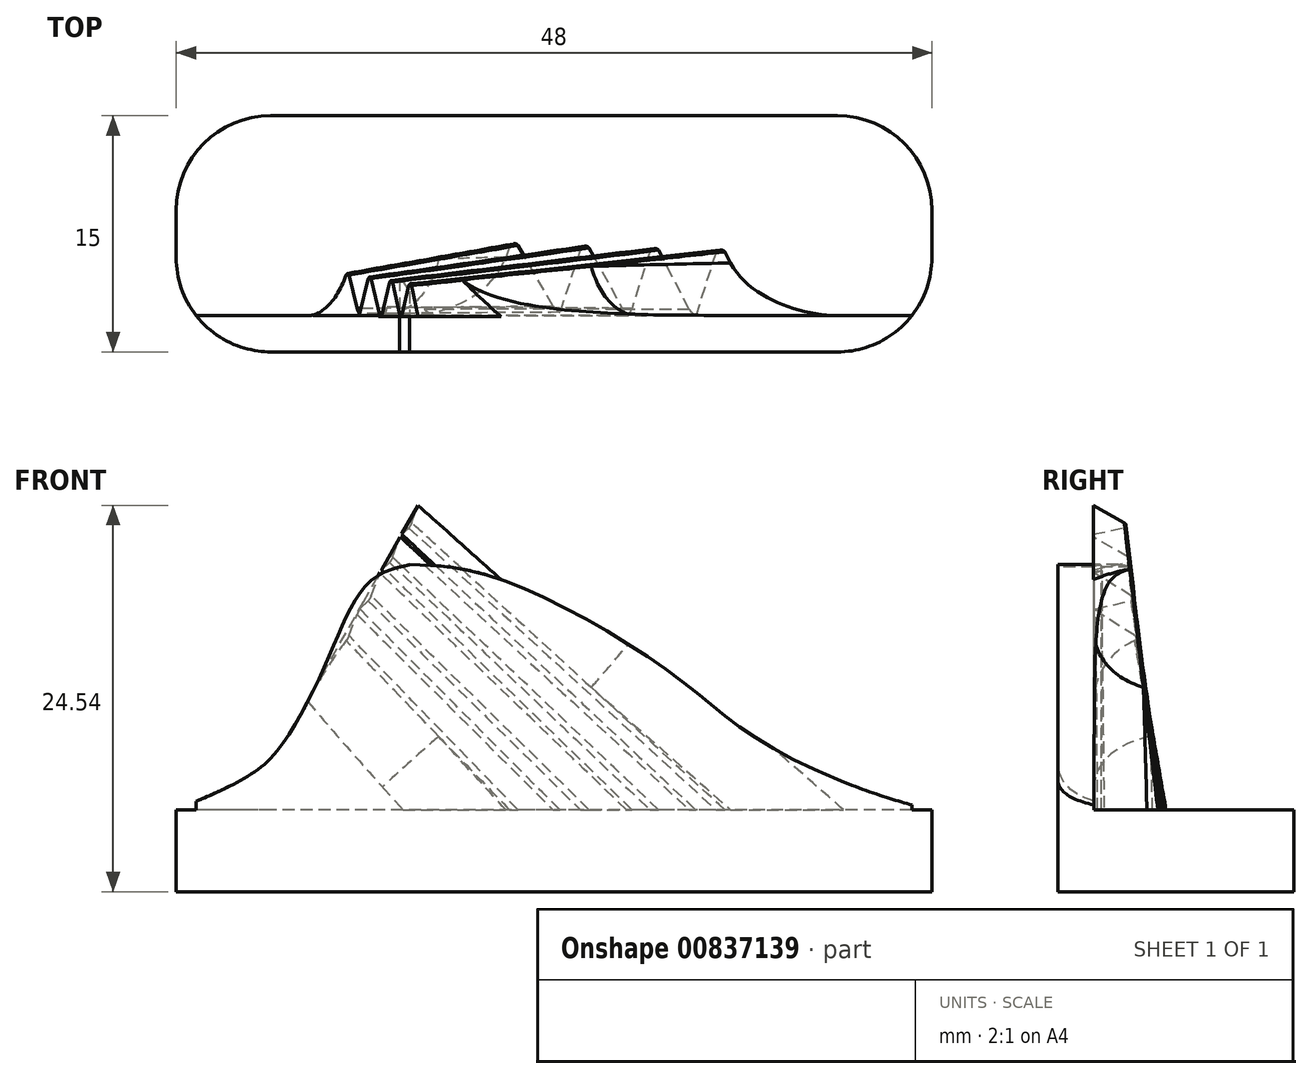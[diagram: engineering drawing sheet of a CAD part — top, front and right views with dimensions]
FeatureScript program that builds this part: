
annotation { "Feature Type Name" : "Feature", "Feature Type Description" : "" }
export const myFeature = defineFeature(function(context is Context, id is Id, definition is map)
    precondition{}
    {
        {
            var Q0;
            Q0=qCreatedBy(makeId("Top.planeOp"),FACE);
            var sketch = newSketch(context, id + "F0", { "sketchPlane" : qUnion([Q0])});
            skLineSegment(sketch, "E0.bottom", {"start": v(18, 7.5) * mm, "end": v(-18, 7.5) * mm});
            skLineSegment(sketch, "E0.top", {"start": v(18, -7.5) * mm, "end": v(-18, -7.5) * mm});
            skLineSegment(sketch, "E0.left", {"start": v(24, 1.5) * mm, "end": v(24, -1.5) * mm});
            skLineSegment(sketch, "E0.right", {"start": v(-24, 1.5) * mm, "end": v(-24, -1.5) * mm});
            skPoint(sketch, "E0.middle", {"position": v(0, 0) * mm});
            skPoint(sketch, "E1.visualSharp", {"position": v(-24, 7.5) * mm});
            skArc(sketch, "E1.filletArc", {"start": v(-18, 7.5) * mm, "mid": v(-22.24, 5.74) * mm, "end": v(-24, 1.5) * mm});
            skPoint(sketch, "E2.visualSharp", {"position": v(-24, -7.5) * mm});
            skArc(sketch, "E2.filletArc", {"start": v(-24, -1.5) * mm, "mid": v(-22.24, -5.74) * mm, "end": v(-18, -7.5) * mm});
            skPoint(sketch, "E3.visualSharp", {"position": v(24, 7.5) * mm});
            skArc(sketch, "E3.filletArc", {"start": v(24, 1.5) * mm, "mid": v(22.24, 5.74) * mm, "end": v(18, 7.5) * mm});
            skPoint(sketch, "E4.visualSharp", {"position": v(24, -7.5) * mm});
            skArc(sketch, "E4.filletArc", {"start": v(18, -7.5) * mm, "mid": v(22.24, -5.74) * mm, "end": v(24, -1.5) * mm});
            skPoint(sketch, "E5", {"position": v(-18, 0) * mm});
            skPoint(sketch, "E6", {"position": v(18, 0) * mm});
            skSolve(sketch);
        }
        {
            var Q0;
            Q0=qCreatedBy(makeId("Right.planeOp"),FACE);
            var sketch = newSketch(context, id + "F1", { "sketchPlane" : qUnion([Q0])});
            skLineSegment(sketch, "E7", {"start": v(-7.5, 0) * mm, "end": v(-7.5, 5.2) * mm});
            skLineSegment(sketch, "E8", {"start": v(-7.5, 5.2) * mm, "end": v(7.5, 5.2) * mm});
            skLineSegment(sketch, "E9", {"start": v(7.5, 5.2) * mm, "end": v(7.5, 0) * mm});
            skLineSegment(sketch, "E10", {"start": v(-7.5, 0) * mm, "end": v(-5.5, 0) * mm});
            skLineSegment(sketch, "E11", {"start": v(7.5, 0) * mm, "end": v(5.5, 0) * mm});
            skLineSegment(sketch, "E12", {"start": v(5.5, 0) * mm, "end": v(-5.5, 0) * mm});
            skSolve(sketch);
        }
        {
            var Q0;
            Q0=makeQuery(id+"F1.imprint","IMPRINT",FACE,{"disambiguationData":[TD([[makeQuery(id+"F1.imprint","IMPRINT",EDGE,{"derivedFrom":sQuery(id+"F1.wireOp",EDGE,"E7")}),-1.0]])]});
            extrude(context, id + "F2", {"entities" : qUnion([Q0]), "endBound" : BoundingType.SYMMETRIC, "depth" : 48 * mm, "offsetDistance" : 25 * mm});
        }
        {
            var Q0;
            Q0=makeQuery(id+"F2.opExtrude","SWEPT_FACE",FACE,{"disambiguationData":[OSD([sQuery(id+"F1.wireOp",EDGE,"E7")])]});
            var sketch = newSketch(context, id + "F3", { "sketchPlane" : qUnion([Q0])});
            skFitSpline(sketch, "E13", {"points": [v(-9.17, 20.78) * mm, v(-1.79, 19.2) * mm, v(7.48, 13.86) * mm, v(13.06, 9.62) * mm, v(24, 5.2) * mm], "startDerivative": vector(37.37, 0) * mm, "endDerivative": vector(42.07, -9.63) * mm});
            skFitSpline(sketch, "E14", {"points": [v(-9.17, 20.78) * mm, v(-11.22, 20.07) * mm, v(-12.79, 18.26) * mm, v(-14.28, 14.96) * mm, v(-16.72, 10.17) * mm, v(-19.07, 7.58) * mm, v(-24, 5.2) * mm], "startDerivative": vector(-16.72, -3.76) * mm, "endDerivative": vector(-25.62, -11.21) * mm});
            skLineSegment(sketch, "E15", {"start": v(-24, 5.2) * mm, "end": v(24, 5.2) * mm});
            skSolve(sketch);
        }
        {
            var Q0;
            {var subQ6=sQuery(id+"F3.wireOp",EDGE,"E13");Q0=makeQuery(id+"F3.imprint","IMPRINT",FACE,{"disambiguationData":[TD([[makeQuery(id+"F3.imprint","IMPRINT",EDGE,{"derivedFrom":subQ6}),-1.0]])]});}
            extrude(context, id + "F4", {"entities" : qUnion([Q0]), "operationType" : NewBodyOperationType.ADD, "oppositeDirection" : true, "depth" : 2.3 * mm, "offsetDistance" : 25 * mm});
        }
        {
            var Q0;
            Q0=makeQuery(id+"F2.opExtrude","CAP_EDGE",EDGE,{"disambiguationData":[OSD([sQuery(id+"F1.wireOp",EDGE,"E7")])],"isStart":true});
            var Q1;
            Q1=makeQuery(id+"F2.opExtrude","CAP_EDGE",EDGE,{"disambiguationData":[OSD([sQuery(id+"F1.wireOp",EDGE,"E7")])],"isStart":false});
            fillet(context, id + "F5", {"entities" : qUnion([Q0, Q1]), "radius" : 6 * mm, "tangentPropagation" : true, "allowEdgeOverflow" : false});
        }
        {
            var Q0;
            Q0=makeQuery(id+"F4.opExtrude","CAP_EDGE",EDGE,{"disambiguationData":[OSD([sQuery(id+"F3.wireOp",EDGE,"E14")])],"isStart":true});
            cPoint(context, id + "F6", {"entities" : qUnion([Q0]), "parameter" : 0.5});
        }
        {
            var Q0;
            Q0=makeQuery(id+"F4.opExtrude","CAP_EDGE",EDGE,{"disambiguationData":[OSD([sQuery(id+"F3.wireOp",EDGE,"E14")])],"isStart":false});
            cPoint(context, id + "F7", {"entities" : qUnion([Q0]), "parameter" : 0.5});
        }
        {
            var Q0;
            {var subQ0=sQuery(id+"F3.wireOp",EDGE,"E14");var subQ1=sQuery(id+"F1.wireOp",EDGE,"E7");Q0=makeQuery(id+"F5.opFillet","BLEND_VERTEX",VERTEX,{"blendedFrom":[makeQuery(id+"F2.opExtrude","CAP_EDGE",EDGE,{"disambiguationData":[OSD([subQ1])],"isStart":true}),makeQuery(id+"F4.opExtrude","SWEPT_FACE",FACE,{"disambiguationData":[OSD([subQ0])]}),makeQuery(id+"F4.boolean.opBoolean","MERGE",FACE,{"derivedFrom":[makeQuery(id+"F2.opExtrude","SWEPT_FACE",FACE,{"disambiguationData":[OSD([subQ1])]}),makeQuery(id+"F4.opExtrude","CAP_FACE",FACE,{"disambiguationData":[OSD([sQuery(id+"F3.wireOp",EDGE,"E13"),subQ0,sQuery(id+"F3.wireOp",EDGE,"E15")])],"isStart":true})]})],"blendedInto":[makeQuery(id+"F4.opExtrude","SWEPT_FACE",FACE,{"disambiguationData":[OSD([subQ0])]}),makeQuery(id+"F4.boolean.opBoolean","MERGE",FACE,{"derivedFrom":[makeQuery(id+"F2.opExtrude","SWEPT_FACE",FACE,{"disambiguationData":[OSD([subQ1])]}),makeQuery(id+"F4.opExtrude","CAP_FACE",FACE,{"disambiguationData":[OSD([sQuery(id+"F3.wireOp",EDGE,"E13"),subQ0,sQuery(id+"F3.wireOp",EDGE,"E15")])],"isStart":true})]})]});}
            var Q1;
            Q1=qCreatedBy(id+"F6",VERTEX);
            var Q2;
            Q2=qCreatedBy(id+"F7",VERTEX);
            cPlane(context, id + "F8", {"entities" : qUnion([Q0, Q1, Q2]), "cplaneType" : CPlaneType.THREE_POINT, "offset" : 25 * mm, "width" : 150 * mm, "height" : 150 * mm});
        }
        {
            var Q0;
            Q0=qCreatedBy(id+"F8.planeOp",FACE);
            var sketch = newSketch(context, id + "F9", { "sketchPlane" : qUnion([Q0])});
            skLineSegment(sketch, "E16", {"start": v(-7.15, 6.5) * mm, "end": v(-4.16, 7.5) * mm});
            skLineSegment(sketch, "E17", {"start": v(-4.16, 7.5) * mm, "end": v(-7.18, 9.5) * mm});
            skLineSegment(sketch, "E18", {"start": v(-7.18, 9.5) * mm, "end": v(-7.15, 6.5) * mm});
            skLineSegment(sketch, "E19", {"start": v(-7.18, 9.5) * mm, "end": v(-4.38, 10.4) * mm});
            skLineSegment(sketch, "E20", {"start": v(-4.38, 10.4) * mm, "end": v(-7.18, 12.2) * mm});
            skLineSegment(sketch, "E21", {"start": v(-7.18, 12.2) * mm, "end": v(-7.18, 9.5) * mm});
            skLineSegment(sketch, "E22", {"start": v(-7.18, 12.4) * mm, "end": v(-4.58, 13.2) * mm});
            skLineSegment(sketch, "E23", {"start": v(-4.58, 13.2) * mm, "end": v(-7.18, 14.8) * mm});
            skLineSegment(sketch, "E24", {"start": v(-7.18, 15) * mm, "end": v(-4.78, 15.7) * mm});
            skLineSegment(sketch, "E25", {"start": v(-4.78, 15.7) * mm, "end": v(-7.18, 17.1) * mm});
            skLineSegment(sketch, "E26", {"start": v(-7.18, 14.8) * mm, "end": v(-7.18, 12.4) * mm});
            skLineSegment(sketch, "E27", {"start": v(-7.18, 15) * mm, "end": v(-7.18, 17.1) * mm});
            skSolve(sketch);
        }
        {
            var Q0;
            Q0=makeQuery(id+"F2.opExtrude","SWEPT_FACE",FACE,{"disambiguationData":[OSD([sQuery(id+"F1.wireOp",EDGE,"E8")])]});
            var sketch = newSketch(context, id + "F10", { "sketchPlane" : qUnion([Q0])});
            skLineSegment(sketch, "E28", {"start": v(13, -5.2) * mm, "end": v(10.5, -0.5) * mm});
            skLineSegment(sketch, "E29", {"start": v(10.5, -0.5) * mm, "end": v(9, -5.2) * mm});
            skLineSegment(sketch, "E30", {"start": v(9, -5.2) * mm, "end": v(13, -5.2) * mm});
            skLineSegment(sketch, "E31", {"start": v(8.8, -5.2) * mm, "end": v(6.3, -0.4) * mm});
            skLineSegment(sketch, "E32", {"start": v(6.3, -0.4) * mm, "end": v(4.8, -5.2) * mm});
            skLineSegment(sketch, "E33", {"start": v(1.9, -0.3) * mm, "end": v(0.3, -5.2) * mm});
            skLineSegment(sketch, "E34", {"start": v(0.3, -5.2) * mm, "end": v(4.6, -5.2) * mm});
            skLineSegment(sketch, "E35", {"start": v(0.3, -5.2) * mm, "end": v(-2.6, -0.2) * mm});
            skLineSegment(sketch, "E36", {"start": v(-2.6, -0.2) * mm, "end": v(-4.4, -5.2) * mm});
            skLineSegment(sketch, "E37", {"start": v(-4.4, -5.2) * mm, "end": v(0.3, -5.2) * mm});
            skLineSegment(sketch, "E38", {"start": v(1.9, -0.3) * mm, "end": v(4.6, -5.2) * mm});
            skLineSegment(sketch, "E39", {"start": v(4.8, -5.2) * mm, "end": v(8.8, -5.2) * mm});
            skSolve(sketch);
        }
        {
            var Q1;
            Q1=makeQuery(id+"F9.imprint","IMPRINT",FACE,{"disambiguationData":[TD([[makeQuery(id+"F9.imprint","IMPRINT",EDGE,{"derivedFrom":sQuery(id+"F9.wireOp",EDGE,"E24")}),1.0]])]});
            var Q2;
            Q2=makeQuery(id+"F10.imprint","IMPRINT",FACE,{"disambiguationData":[TD([[makeQuery(id+"F10.imprint","IMPRINT",EDGE,{"derivedFrom":sQuery(id+"F10.wireOp",EDGE,"E28")}),1.0]])]});
            loft(context, id + "F11", {"operationType" : NewBodyOperationType.ADD, "sheetProfilesArray" : [{ "sheetProfileEntities" : qUnion([Q1]) }, { "sheetProfileEntities" : qUnion([Q2]) }]});
        }
        {
            var Q1;
            Q1=makeQuery(id+"F10.imprint","IMPRINT",FACE,{"disambiguationData":[TD([[makeQuery(id+"F10.imprint","IMPRINT",EDGE,{"derivedFrom":sQuery(id+"F10.wireOp",EDGE,"E33")}),1.0]])]});
            var Q2;
            Q2=makeQuery(id+"F9.imprint","IMPRINT",FACE,{"disambiguationData":[TD([[makeQuery(id+"F9.imprint","IMPRINT",EDGE,{"derivedFrom":sQuery(id+"F9.wireOp",EDGE,"E19")}),1.0]])]});
            loft(context, id + "F12", {"operationType" : NewBodyOperationType.ADD, "sheetProfilesArray" : [{ "sheetProfileEntities" : qUnion([Q1]) }, { "sheetProfileEntities" : qUnion([Q2]) }]});
        }
        {
            var Q1;
            Q1=makeQuery(id+"F9.imprint","IMPRINT",FACE,{"disambiguationData":[TD([[makeQuery(id+"F9.imprint","IMPRINT",EDGE,{"derivedFrom":sQuery(id+"F9.wireOp",EDGE,"E16")}),1.0]])]});
            var Q2;
            Q2=makeQuery(id+"F10.imprint","IMPRINT",FACE,{"disambiguationData":[TD([[makeQuery(id+"F10.imprint","IMPRINT",EDGE,{"derivedFrom":sQuery(id+"F10.wireOp",EDGE,"E35")}),1.0]])]});
            loft(context, id + "F13", {"operationType" : NewBodyOperationType.ADD, "sheetProfilesArray" : [{ "sheetProfileEntities" : qUnion([Q1]) }, { "sheetProfileEntities" : qUnion([Q2]) }]});
        }
        {
            var Q1;
            Q1=makeQuery(id+"F9.imprint","IMPRINT",FACE,{"disambiguationData":[TD([[makeQuery(id+"F9.imprint","IMPRINT",EDGE,{"derivedFrom":sQuery(id+"F9.wireOp",EDGE,"E22")}),1.0]])]});
            var Q2;
            Q2=makeQuery(id+"F10.imprint","IMPRINT",FACE,{"disambiguationData":[TD([[makeQuery(id+"F10.imprint","IMPRINT",EDGE,{"derivedFrom":sQuery(id+"F10.wireOp",EDGE,"E31")}),1.0]])]});
            loft(context, id + "F14", {"operationType" : NewBodyOperationType.ADD, "sheetProfilesArray" : [{ "sheetProfileEntities" : qUnion([Q1]) }, { "sheetProfileEntities" : qUnion([Q2]) }]});
        }
        {
            var Q0;
            Q0=makeQuery(id+"F13.opLoft","SWEPT_EDGE",EDGE,{"disambiguationData":[OSD([sQuery(id+"F9.wireOp",EDGE,"E16"),sQuery(id+"F9.wireOp",EDGE,"E17"),sQuery(id+"F10.wireOp",EDGE,"E35"),sQuery(id+"F10.wireOp",EDGE,"E36")])]});
            var Q1;
            Q1=makeQuery(id+"F12.opLoft","SWEPT_EDGE",EDGE,{"disambiguationData":[OSD([sQuery(id+"F9.wireOp",EDGE,"E19"),sQuery(id+"F9.wireOp",EDGE,"E20"),sQuery(id+"F10.wireOp",EDGE,"E33"),sQuery(id+"F10.wireOp",EDGE,"E38")])]});
            var Q2;
            Q2=makeQuery(id+"F14.opLoft","SWEPT_EDGE",EDGE,{"disambiguationData":[OSD([sQuery(id+"F9.wireOp",EDGE,"E22"),sQuery(id+"F9.wireOp",EDGE,"E23"),sQuery(id+"F10.wireOp",EDGE,"E31"),sQuery(id+"F10.wireOp",EDGE,"E32")])]});
            var Q3;
            Q3=makeQuery(id+"F11.opLoft","SWEPT_EDGE",EDGE,{"disambiguationData":[OSD([sQuery(id+"F9.wireOp",EDGE,"E24"),sQuery(id+"F9.wireOp",EDGE,"E25"),sQuery(id+"F10.wireOp",EDGE,"E28"),sQuery(id+"F10.wireOp",EDGE,"E29")])]});
            fillet(context, id + "F15", {"entities" : qUnion([Q0, Q1, Q2, Q3]), "radius" : 0.2 * mm, "tangentPropagation" : true, "allowEdgeOverflow" : false});
        }
        {
            var Q0;
            {var subQ0=sQuery(id+"F10.wireOp",EDGE,"E37");var subQ1=sQuery(id+"F10.wireOp",EDGE,"E35");var subQ2=sQuery(id+"F9.wireOp",EDGE,"E18");var subQ3=sQuery(id+"F9.wireOp",EDGE,"E17");var subQ4=sQuery(id+"F3.wireOp",EDGE,"E15");var subQ8=sQuery(id+"F1.wireOp",EDGE,"E7");var subQ9=makeQuery(id+"F5.opFillet","BLEND_FACE",FACE,{"disambiguationData":[OSD([subQ8]),TDD([makeQuery(id+"F2.opExtrude","CAP_EDGE",EDGE,{"disambiguationData":[OSD([subQ8])],"isStart":true})])]});var subQ10=sQuery(id+"F3.wireOp",EDGE,"E14");var subQ11=makeQuery(id+"F4.opExtrude","SWEPT_FACE",FACE,{"disambiguationData":[OSD([subQ10])]});var subQ13=sQuery(id+"F3.wireOp",EDGE,"E13");Q0=makeQuery(id+"F13.boolean.opBoolean","INTERSECT",EDGE,{"derivedFrom":[makeQuery(id+"F12.boolean.opBoolean","SPLIT",FACE,{"disambiguationData":[TD([subQ9])],"derivedFrom":makeQuery(id+"F11.boolean.opBoolean","SPLIT",FACE,{"disambiguationData":[TD([subQ11])],"derivedFrom":makeQuery(id+"F4.opExtrude","CAP_FACE",FACE,{"disambiguationData":[OSD([subQ13,subQ10,subQ4])],"isStart":false})})}),makeQuery(id+"F13.opLoft","SWEPT_FACE",FACE,{"disambiguationData":[OSD([subQ4,sQuery(id+"F9.wireOp",EDGE,"E16"),subQ3,subQ2,subQ1,sQuery(id+"F10.wireOp",EDGE,"E36"),subQ0])]})]});}
            var Q1;
            {var subQ0=sQuery(id+"F10.wireOp",EDGE,"E28");var subQ1=sQuery(id+"F10.wireOp",EDGE,"E29");var subQ2=sQuery(id+"F10.wireOp",EDGE,"E30");var subQ3=sQuery(id+"F3.wireOp",EDGE,"E15");var subQ4=sQuery(id+"F9.wireOp",EDGE,"E25");var subQ5=sQuery(id+"F9.wireOp",EDGE,"E27");var subQ6=sQuery(id+"F9.wireOp",EDGE,"E24");Q1=makeQuery(id+"F11.boolean.opBoolean","INTERSECT",EDGE,{"derivedFrom":[makeQuery(id+"F4.opExtrude","CAP_FACE",FACE,{"disambiguationData":[OSD([sQuery(id+"F3.wireOp",EDGE,"E13"),sQuery(id+"F3.wireOp",EDGE,"E14"),subQ3])],"isStart":false}),makeQuery(id+"F11.opLoft","SWEPT_FACE",FACE,{"disambiguationData":[OSD([subQ3,subQ6,subQ4,subQ5,subQ0,subQ1,subQ2]),TDD([makeQuery(id+"F9.imprint","INTERSECT",VERTEX,{"derivedFrom":[subQ6,subQ4]}),makeQuery(id+"F9.imprint","INTERSECT",VERTEX,{"derivedFrom":[subQ4,subQ5]}),makeQuery(id+"F9.imprint","IMPRINT",EDGE,{"derivedFrom":subQ4}),makeQuery(id+"F10.imprint","INTERSECT",VERTEX,{"derivedFrom":[makeQuery(id+"F4.opExtrude","CAP_EDGE",EDGE,{"disambiguationData":[OSD([subQ3])],"isStart":false}),subQ0,subQ2]}),makeQuery(id+"F10.imprint","INTERSECT",VERTEX,{"derivedFrom":[subQ0,subQ1]}),makeQuery(id+"F10.imprint","IMPRINT",EDGE,{"derivedFrom":subQ0})])]})]});}
            fillet(context, id + "F16", {"entities" : qUnion([Q0, Q1]), "radius" : 5 * mm, "tangentPropagation" : true, "allowEdgeOverflow" : false});
        }
        {
            var Q0;
            {var subQ0=sQuery(id+"F10.wireOp",EDGE,"E37");var subQ1=sQuery(id+"F10.wireOp",EDGE,"E35");var subQ2=sQuery(id+"F10.wireOp",EDGE,"E34");var subQ3=sQuery(id+"F10.wireOp",EDGE,"E33");var subQ4=sQuery(id+"F9.wireOp",EDGE,"E21");var subQ5=sQuery(id+"F9.wireOp",EDGE,"E19");var subQ6=sQuery(id+"F9.wireOp",EDGE,"E18");var subQ7=sQuery(id+"F9.wireOp",EDGE,"E17");var subQ9=sQuery(id+"F1.wireOp",EDGE,"E7");var subQ10=makeQuery(id+"F5.opFillet","BLEND_FACE",FACE,{"disambiguationData":[OSD([subQ9]),TDD([makeQuery(id+"F2.opExtrude","CAP_EDGE",EDGE,{"disambiguationData":[OSD([subQ9])],"isStart":true})])]});var subQ11=sQuery(id+"F3.wireOp",EDGE,"E14");var subQ12=makeQuery(id+"F4.opExtrude","SWEPT_FACE",FACE,{"disambiguationData":[OSD([subQ11])]});var subQ14=sQuery(id+"F3.wireOp",EDGE,"E13");var subQ17=sQuery(id+"F3.wireOp",EDGE,"E15");Q0=makeQuery(id+"F13.boolean.opBoolean","INTERSECT",EDGE,{"derivedFrom":[makeQuery(id+"F12.boolean.opBoolean","SPLIT",FACE,{"disambiguationData":[TD([subQ10])],"derivedFrom":makeQuery(id+"F11.boolean.opBoolean","SPLIT",FACE,{"disambiguationData":[TD([subQ12])],"derivedFrom":makeQuery(id+"F4.opExtrude","CAP_FACE",FACE,{"disambiguationData":[OSD([subQ14,subQ11,subQ17])],"isStart":false})})}),makeQuery(id+"F13.opLoft","SWEPT_FACE",FACE,{"disambiguationData":[OSD([sQuery(id+"F9.wireOp",EDGE,"E16"),subQ7,subQ6,subQ5,subQ4,subQ3,subQ2,subQ1,sQuery(id+"F10.wireOp",EDGE,"E36"),subQ0])]})]});}
            var Q1;
            {var subQ0=sQuery(id+"F10.wireOp",EDGE,"E32");var subQ1=sQuery(id+"F10.wireOp",EDGE,"E39");var subQ2=sQuery(id+"F3.wireOp",EDGE,"E15");var subQ3=makeQuery(id+"F4.opExtrude","CAP_EDGE",EDGE,{"disambiguationData":[OSD([subQ2])],"isStart":false});var subQ4=sQuery(id+"F10.wireOp",EDGE,"E31");var subQ5=sQuery(id+"F9.wireOp",EDGE,"E22");var subQ6=sQuery(id+"F9.wireOp",EDGE,"E23");var subQ7=sQuery(id+"F9.wireOp",EDGE,"E26");var subQ8=sQuery(id+"F3.wireOp",EDGE,"E14");var subQ9=makeQuery(id+"F4.opExtrude","SWEPT_FACE",FACE,{"disambiguationData":[OSD([subQ8])]});var subQ17=sQuery(id+"F3.wireOp",EDGE,"E13");var subQ18=makeQuery(id+"F4.opExtrude","SWEPT_FACE",FACE,{"disambiguationData":[OSD([subQ17])]});Q1=makeQuery(id+"F14.boolean.opBoolean","INTERSECT",EDGE,{"derivedFrom":[makeQuery(id+"F12.boolean.opBoolean","SPLIT",FACE,{"disambiguationData":[TD([subQ18])],"derivedFrom":makeQuery(id+"F11.boolean.opBoolean","SPLIT",FACE,{"disambiguationData":[TD([subQ9])],"derivedFrom":makeQuery(id+"F4.opExtrude","CAP_FACE",FACE,{"disambiguationData":[OSD([subQ17,subQ8,subQ2])],"isStart":false})})}),makeQuery(id+"F14.opLoft","SWEPT_FACE",FACE,{"disambiguationData":[OSD([subQ2,subQ5,subQ6,subQ7,subQ4,subQ0,subQ1]),TDD([makeQuery(id+"F9.imprint","INTERSECT",VERTEX,{"derivedFrom":[subQ5,subQ7]}),makeQuery(id+"F9.imprint","INTERSECT",VERTEX,{"derivedFrom":[subQ5,subQ6]}),makeQuery(id+"F9.imprint","IMPRINT",EDGE,{"derivedFrom":subQ5}),makeQuery(id+"F10.imprint","INTERSECT",VERTEX,{"derivedFrom":[subQ4,subQ0]}),makeQuery(id+"F10.imprint","INTERSECT",VERTEX,{"derivedFrom":[subQ3,subQ0,subQ1]}),makeQuery(id+"F10.imprint","IMPRINT",EDGE,{"derivedFrom":subQ0})])]})]});}
            var Q2;
            {var subQ0=sQuery(id+"F10.wireOp",EDGE,"E31");var subQ1=sQuery(id+"F10.wireOp",EDGE,"E32");var subQ2=sQuery(id+"F10.wireOp",EDGE,"E39");var subQ3=sQuery(id+"F3.wireOp",EDGE,"E15");var subQ4=makeQuery(id+"F4.opExtrude","CAP_EDGE",EDGE,{"disambiguationData":[OSD([subQ3])],"isStart":false});var subQ5=sQuery(id+"F9.wireOp",EDGE,"E23");var subQ6=sQuery(id+"F9.wireOp",EDGE,"E26");var subQ7=sQuery(id+"F9.wireOp",EDGE,"E22");var subQ8=sQuery(id+"F3.wireOp",EDGE,"E14");var subQ9=makeQuery(id+"F4.opExtrude","SWEPT_FACE",FACE,{"disambiguationData":[OSD([subQ8])]});var subQ17=sQuery(id+"F3.wireOp",EDGE,"E13");var subQ18=makeQuery(id+"F4.opExtrude","SWEPT_FACE",FACE,{"disambiguationData":[OSD([subQ17])]});Q2=makeQuery(id+"F14.boolean.opBoolean","INTERSECT",EDGE,{"derivedFrom":[makeQuery(id+"F12.boolean.opBoolean","SPLIT",FACE,{"disambiguationData":[TD([subQ18])],"derivedFrom":makeQuery(id+"F11.boolean.opBoolean","SPLIT",FACE,{"disambiguationData":[TD([subQ9])],"derivedFrom":makeQuery(id+"F4.opExtrude","CAP_FACE",FACE,{"disambiguationData":[OSD([subQ17,subQ8,subQ3])],"isStart":false})})}),makeQuery(id+"F14.opLoft","SWEPT_FACE",FACE,{"disambiguationData":[OSD([subQ3,subQ7,subQ5,subQ6,subQ0,subQ1,subQ2]),TDD([makeQuery(id+"F9.imprint","INTERSECT",VERTEX,{"derivedFrom":[subQ7,subQ5]}),makeQuery(id+"F9.imprint","INTERSECT",VERTEX,{"derivedFrom":[subQ5,subQ6]}),makeQuery(id+"F9.imprint","IMPRINT",EDGE,{"derivedFrom":subQ5}),makeQuery(id+"F10.imprint","INTERSECT",VERTEX,{"derivedFrom":[subQ4,subQ0,subQ2]}),makeQuery(id+"F10.imprint","INTERSECT",VERTEX,{"derivedFrom":[subQ0,subQ1]}),makeQuery(id+"F10.imprint","IMPRINT",EDGE,{"derivedFrom":subQ0})])]})]});}
            fillet(context, id + "F17", {"entities" : qUnion([Q0, Q1, Q2]), "radius" : 1 * mm, "tangentPropagation" : true, "allowEdgeOverflow" : false});
        }
        {
            var Q0;
            Q0=makeQuery(id+"F2.opExtrude","CAP_EDGE",EDGE,{"disambiguationData":[OSD([sQuery(id+"F1.wireOp",EDGE,"E9")])],"isStart":false});
            var Q1;
            Q1=makeQuery(id+"F2.opExtrude","CAP_EDGE",EDGE,{"disambiguationData":[OSD([sQuery(id+"F1.wireOp",EDGE,"E9")])],"isStart":true});
            fillet(context, id + "F18", {"entities" : qUnion([Q0, Q1]), "radius" : 6 * mm, "tangentPropagation" : true, "allowEdgeOverflow" : false});
        }
        {
            var Q0;
            Q0=makeQuery(id+"F4.boolean.opBoolean","MERGE",FACE,{"derivedFrom":[makeQuery(id+"F2.opExtrude","SWEPT_FACE",FACE,{"disambiguationData":[OSD([sQuery(id+"F1.wireOp",EDGE,"E7")])]}),makeQuery(id+"F4.opExtrude","CAP_FACE",FACE,{"disambiguationData":[OSD([sQuery(id+"F3.wireOp",EDGE,"E13"),sQuery(id+"F3.wireOp",EDGE,"E14"),sQuery(id+"F3.wireOp",EDGE,"E15")])],"isStart":true})]});
            var sketch = newSketch(context, id + "F19", { "sketchPlane" : qUnion([Q0])});
            skFitSpline(sketch, "E40.0", {"points": [v(-9.17, 20.78) * mm, v(-9.89, 20.62) * mm, v(-11.37, 20.28) * mm, v(-12.98, 18.22) * mm, v(-14.22, 14.92) * mm, v(-16.6, 10.04) * mm, v(-18.84, 7.3) * mm, v(-22.26, 5.96) * mm, v(-24, 5.2) * mm]});
            skFitSpline(sketch, "E41.0", {"points": [v(-9.17, 20.78) * mm, v(-6.34, 20.78) * mm, v(-1.89, 19.72) * mm, v(7.9, 14.01) * mm, v(12.65, 9.21) * mm, v(20.02, 6.11) * mm, v(24, 5.2) * mm]});
            skLineSegment(sketch, "E42", {"start": v(-18, 8.47) * mm, "end": v(-18, 26.91) * mm});
            skLineSegment(sketch, "E43", {"start": v(-18, 26.91) * mm, "end": v(18, 26.91) * mm});
            skLineSegment(sketch, "E44", {"start": v(18, 26.91) * mm, "end": v(18, 7.13) * mm});
            skSolve(sketch);
        }
        {
            var Q0;
            Q0=makeQuery(id+"F19.imprint","IMPRINT",FACE,{"disambiguationData":[TD([[makeQuery(id+"F19.imprint","IMPRINT",EDGE,{"derivedFrom":sQuery(id+"F19.wireOp",EDGE,"E40.0")}),-1.0]])]});
            extrude(context, id + "F20", {"entities" : qUnion([Q0]), "operationType" : NewBodyOperationType.REMOVE, "endBound" : BoundingType.THROUGH_ALL, "oppositeDirection" : true, "depth" : 25 * mm, "offsetDistance" : 25 * mm});
        }
    });
